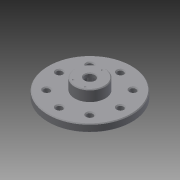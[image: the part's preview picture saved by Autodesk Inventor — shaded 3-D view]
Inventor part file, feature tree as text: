
AUTODESK INVENTOR PART (.ipt)
format: ipt  version: 2016 (Build 200138000, 138)  size: 393,216 bytes
history: native  units: in
note: dims shown in document units (in); Inventor stores cm internally (conversion verified against a paired STEP export)
features: other x3, sketch x2
ambient origin geometry x8: Origin, YZ Plane, XZ Plane, XY Plane, X Axis, Y Axis, Z Axis, Center Point
bodies: Solid1 (feature_tree)
feature tree (5):
  other  "HN07-N101.ipt"
  other  "Solid1::HN07-N101.ipt"
  other  "TaggingFeature1"
  sketch  "Sketch2"  dims[d0=0.3937in]
  sketch  "Sketch3"  dims[d1=0.2244in d8=0.2244in]
